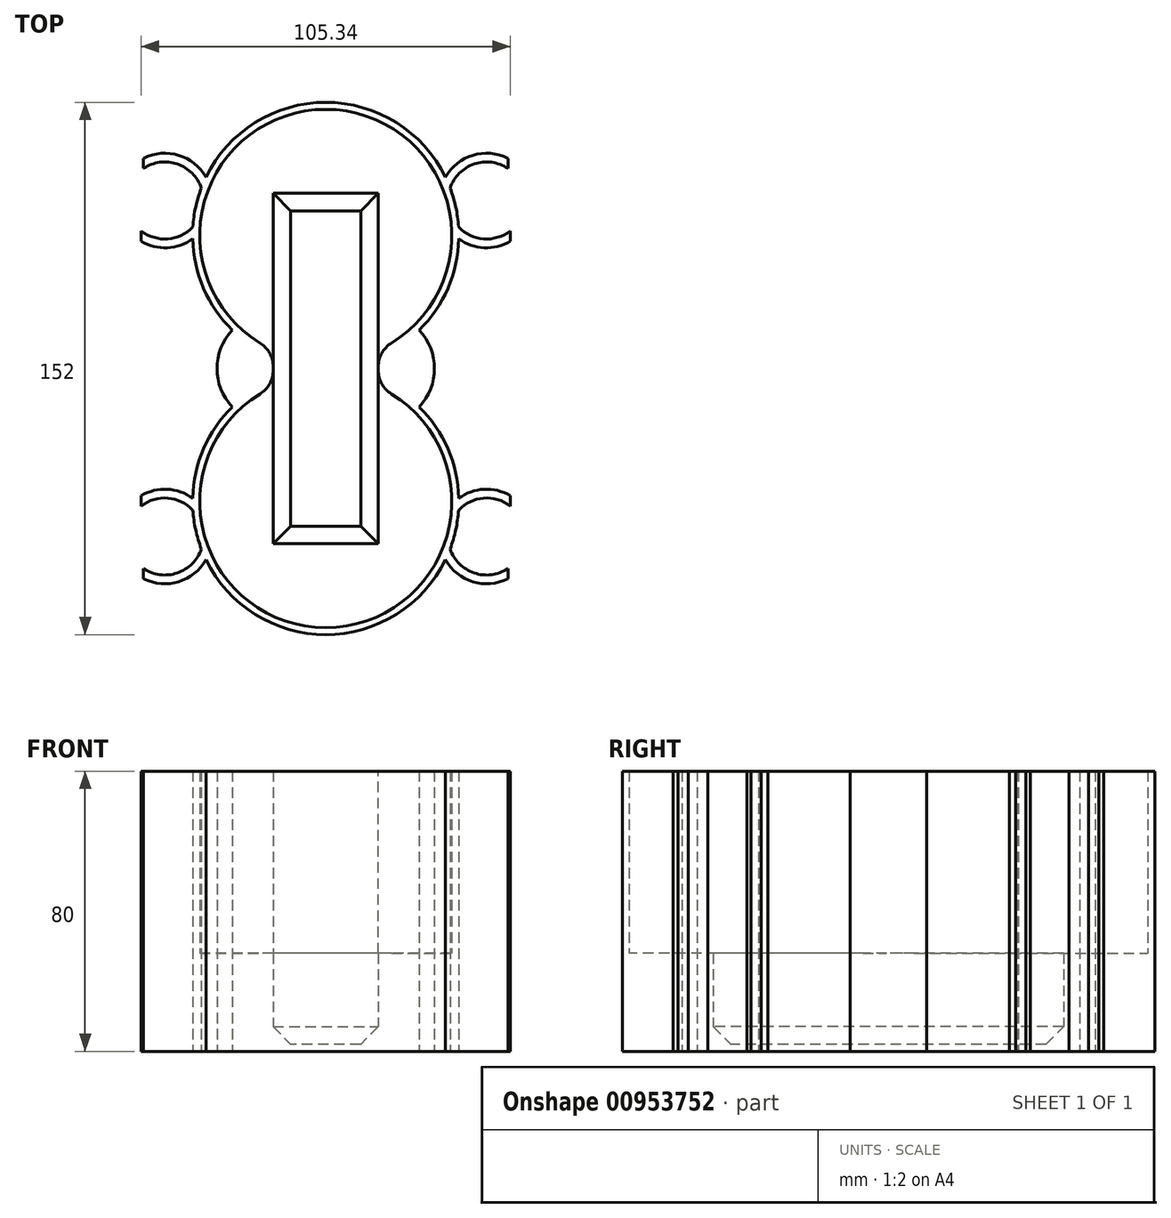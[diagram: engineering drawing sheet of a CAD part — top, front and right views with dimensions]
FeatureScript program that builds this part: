
annotation { "Feature Type Name" : "Feature", "Feature Type Description" : "" }
export const myFeature = defineFeature(function(context is Context, id is Id, definition is map)
    precondition{}
    {
        {
            var Q0;
            Q0=qCreatedBy(makeId("Top.planeOp"),FACE);
            var sketch = newSketch(context, id + "F0", { "sketchPlane" : qUnion([Q0])});
            skCircle(sketch, "E0", {"center": v(0, 38) * mm, "radius": 36 * mm});
            skCircle(sketch, "E1", {"center": v(0, 38) * mm, "radius": 38 * mm});
            skCircle(sketch, "E2", {"center": v(0, -38) * mm, "radius": 38 * mm});
            skCircle(sketch, "E3", {"center": v(0, -38) * mm, "radius": 36 * mm});
            skLineSegment(sketch, "E4.bottom", {"start": v(15, 50) * mm, "end": v(-15, 50) * mm});
            skLineSegment(sketch, "E4.top", {"start": v(15, -50) * mm, "end": v(-15, -50) * mm});
            skLineSegment(sketch, "E4.left", {"start": v(15, 50) * mm, "end": v(15, -50) * mm});
            skLineSegment(sketch, "E4.right", {"start": v(-15, 50) * mm, "end": v(-15, -50) * mm});
            skPoint(sketch, "E4.middle", {"position": v(0, 0) * mm});
            skArc(sketch, "E5", {"start": v(-26.7, 10.97) * mm, "mid": v(-31.04, 0) * mm, "end": v(-26.7, -10.97) * mm});
            skArc(sketch, "E6", {"start": v(26.7, -10.97) * mm, "mid": v(31.04, 0) * mm, "end": v(26.7, 10.97) * mm});
            skArc(sketch, "E7", {"start": v(-52.67, 39.29) * mm, "mid": v(-34.94, 47.58) * mm, "end": v(-52.02, 57.14) * mm});
            skArc(sketch, "E8", {"start": v(-33.1, 52.17) * mm, "mid": v(-40.75, 60.45) * mm, "end": v(-52.02, 60.03) * mm});
            skLineSegment(sketch, "E9", {"start": v(-52.02, 60.03) * mm, "end": v(-52.02, 57.14) * mm});
            skLineSegment(sketch, "E10", {"start": v(-52.67, 39.29) * mm, "end": v(-52.67, 36.28) * mm});
            skArc(sketch, "E11.trimOffspring", {"start": v(-52.67, 36.28) * mm, "mid": v(-43.88, 34.64) * mm, "end": v(-36, 38.84) * mm});
            skArc(sketch, "E12.MirrorCS", {"start": v(52.67, 39.29) * mm, "mid": v(34.94, 47.58) * mm, "end": v(52.02, 57.14) * mm});
            skArc(sketch, "E13.MirrorCS", {"start": v(33.1, 52.17) * mm, "mid": v(40.75, 60.45) * mm, "end": v(52.02, 60.03) * mm});
            skArc(sketch, "E14.MirrorCS", {"start": v(52.67, 36.28) * mm, "mid": v(43.88, 34.64) * mm, "end": v(36, 38.84) * mm});
            skLineSegment(sketch, "E15.MirrorCS", {"start": v(52.67, 39.29) * mm, "end": v(52.67, 36.28) * mm});
            skLineSegment(sketch, "E16.MirrorCS", {"start": v(52.02, 60.03) * mm, "end": v(52.02, 57.14) * mm});
            skArc(sketch, "E17.MirrorCS", {"start": v(-52.67, -36.28) * mm, "mid": v(-43.88, -34.64) * mm, "end": v(-36, -38.84) * mm});
            skArc(sketch, "E18.MirrorCS", {"start": v(-52.67, -39.29) * mm, "mid": v(-34.94, -47.58) * mm, "end": v(-52.02, -57.14) * mm});
            skArc(sketch, "E19.MirrorCS", {"start": v(-33.1, -52.17) * mm, "mid": v(-40.75, -60.45) * mm, "end": v(-52.02, -60.03) * mm});
            skLineSegment(sketch, "E20.MirrorCS", {"start": v(-52.02, -60.03) * mm, "end": v(-52.02, -57.14) * mm});
            skLineSegment(sketch, "E21.MirrorCS", {"start": v(-52.67, -39.29) * mm, "end": v(-52.67, -36.28) * mm});
            skArc(sketch, "E22.MirrorCS", {"start": v(52.67, -36.28) * mm, "mid": v(43.88, -34.64) * mm, "end": v(36, -38.84) * mm});
            skArc(sketch, "E23.MirrorCS", {"start": v(52.67, -39.29) * mm, "mid": v(34.94, -47.58) * mm, "end": v(52.02, -57.14) * mm});
            skArc(sketch, "E24.MirrorCS", {"start": v(33.1, -52.17) * mm, "mid": v(40.75, -60.45) * mm, "end": v(52.02, -60.03) * mm});
            skLineSegment(sketch, "E25.MirrorCS", {"start": v(52.02, -60.03) * mm, "end": v(52.02, -57.14) * mm});
            skLineSegment(sketch, "E26.MirrorCS", {"start": v(52.67, -39.29) * mm, "end": v(52.67, -36.28) * mm});
            skSolve(sketch);
        }
        {
            var Q0;
            Q0 = qSketchRegion(id + "F0", true);
            extrude(context, id + "F1", {"entities" : qUnion([Q0]), "depth" : 80 * mm, "offsetDistance" : 25 * mm});
        }
        {
            var Q0;
            {var subQ5=sQuery(id+"F0.wireOp",EDGE,"E4.bottom");Q0=makeQuery(id+"F0.imprint","IMPRINT",FACE,{"disambiguationData":[TD([[makeQuery(id+"F0.imprint","IMPRINT",EDGE,{"derivedFrom":subQ5}),-1.0]])]});}
            var Q1;
            {var subQ5=sQuery(id+"F0.wireOp",EDGE,"E4.top");Q1=makeQuery(id+"F0.imprint","IMPRINT",FACE,{"disambiguationData":[TD([[makeQuery(id+"F0.imprint","IMPRINT",EDGE,{"derivedFrom":subQ5}),1.0]])]});}
            extrude(context, id + "F2", {"entities" : qUnion([Q0, Q1]), "operationType" : NewBodyOperationType.ADD, "depth" : 28 * mm, "offsetDistance" : 25 * mm});
        }
        {
            var Q0;
            {var subQ5=sQuery(id+"F0.wireOp",EDGE,"E4.bottom");Q0=makeQuery(id+"F0.imprint","IMPRINT",FACE,{"disambiguationData":[TD([[makeQuery(id+"F0.imprint","IMPRINT",EDGE,{"derivedFrom":subQ5}),1.0]])]});}
            var Q1;
            {var subQ5=sQuery(id+"F0.wireOp",EDGE,"E4.top");Q1=makeQuery(id+"F0.imprint","IMPRINT",FACE,{"disambiguationData":[TD([[makeQuery(id+"F0.imprint","IMPRINT",EDGE,{"derivedFrom":subQ5}),-1.0]])]});}
            var Q2;
            {var subQ0=sQuery(id+"F0.wireOp",EDGE,"E4.right");var subQ1=sQuery(id+"F0.wireOp",EDGE,"E1");var subQ2=makeQuery(id+"F0.imprint","INTERSECT",VERTEX,{"derivedFrom":[subQ1,subQ0]});Q2=makeQuery(id+"F0.imprint","IMPRINT",FACE,{"disambiguationData":[TD([[makeQuery(id+"F0.imprint","IMPRINT",EDGE,{"disambiguationData":[TD([[subQ2,-1.0]])],"derivedFrom":subQ1}),-1.0]])]});}
            var Q3;
            {var subQ0=sQuery(id+"F0.wireOp",EDGE,"E4.left");var subQ1=sQuery(id+"F0.wireOp",EDGE,"E0");var subQ2=makeQuery(id+"F0.imprint","INTERSECT",VERTEX,{"derivedFrom":[subQ1,subQ0]});Q3=makeQuery(id+"F0.imprint","IMPRINT",FACE,{"disambiguationData":[TD([[makeQuery(id+"F0.imprint","IMPRINT",EDGE,{"disambiguationData":[TD([[subQ2,1.0]])],"derivedFrom":subQ1}),-1.0]])]});}
            var Q4;
            {var subQ0=sQuery(id+"F0.wireOp",EDGE,"E4.left");var subQ1=sQuery(id+"F0.wireOp",EDGE,"E2");var subQ2=makeQuery(id+"F0.imprint","INTERSECT",VERTEX,{"derivedFrom":[subQ1,subQ0]});Q4=makeQuery(id+"F0.imprint","IMPRINT",FACE,{"disambiguationData":[TD([[makeQuery(id+"F0.imprint","IMPRINT",EDGE,{"disambiguationData":[TD([[subQ2,-1.0]])],"derivedFrom":subQ1}),1.0]])]});}
            var Q5;
            {var subQ0=sQuery(id+"F0.wireOp",EDGE,"E2");var subQ1=sQuery(id+"F0.wireOp",EDGE,"E1");var subQ2=makeQuery(id+"F0.imprint","INTERSECT",VERTEX,{"derivedFrom":[subQ1,subQ0]});Q5=makeQuery(id+"F0.imprint","IMPRINT",FACE,{"disambiguationData":[TD([[makeQuery(id+"F0.imprint","IMPRINT",EDGE,{"disambiguationData":[TD([[subQ2,-1.0]])],"derivedFrom":subQ1}),-1.0]])]});}
            extrude(context, id + "F3", {"entities" : qUnion([Q0, Q1, Q2, Q3, Q4, Q5]), "operationType" : NewBodyOperationType.ADD, "depth" : 2 * mm, "offsetDistance" : 25 * mm});
        }
        {
            var Q0;
            Q0=makeQuery(id+"F3.opExtrude","CAP_FACE",FACE,{"disambiguationData":[OSD([sQuery(id+"F0.wireOp",EDGE,"E4.bottom"),sQuery(id+"F0.wireOp",EDGE,"E4.top"),sQuery(id+"F0.wireOp",EDGE,"E4.left"),sQuery(id+"F0.wireOp",EDGE,"E4.right")])],"isStart":false});
            chamfer(context, id + "F4", {"entities" : qUnion([Q0]), "width" : 5 * mm, "tangentPropagation" : true});
        }
        {
            var Q0;
            Q0=makeQuery(id+"F1.opExtrude","SWEPT_EDGE",EDGE,{"disambiguationData":[OSD([sQuery(id+"F0.wireOp",EDGE,"E3"),sQuery(id+"F0.wireOp",EDGE,"E4.right")])]});
            var Q1;
            Q1=makeQuery(id+"F1.opExtrude","SWEPT_EDGE",EDGE,{"disambiguationData":[OSD([sQuery(id+"F0.wireOp",EDGE,"E0"),sQuery(id+"F0.wireOp",EDGE,"E4.right")])]});
            var Q2;
            Q2=makeQuery(id+"F1.opExtrude","SWEPT_EDGE",EDGE,{"disambiguationData":[OSD([sQuery(id+"F0.wireOp",EDGE,"E3"),sQuery(id+"F0.wireOp",EDGE,"E4.left")])]});
            var Q3;
            Q3=makeQuery(id+"F1.opExtrude","SWEPT_EDGE",EDGE,{"disambiguationData":[OSD([sQuery(id+"F0.wireOp",EDGE,"E0"),sQuery(id+"F0.wireOp",EDGE,"E4.left")])]});
            fillet(context, id + "F5", {"entities" : qUnion([Q0, Q1, Q2, Q3]), "radius" : 8 * mm, "tangentPropagation" : true, "allowEdgeOverflow" : false});
        }
    });
